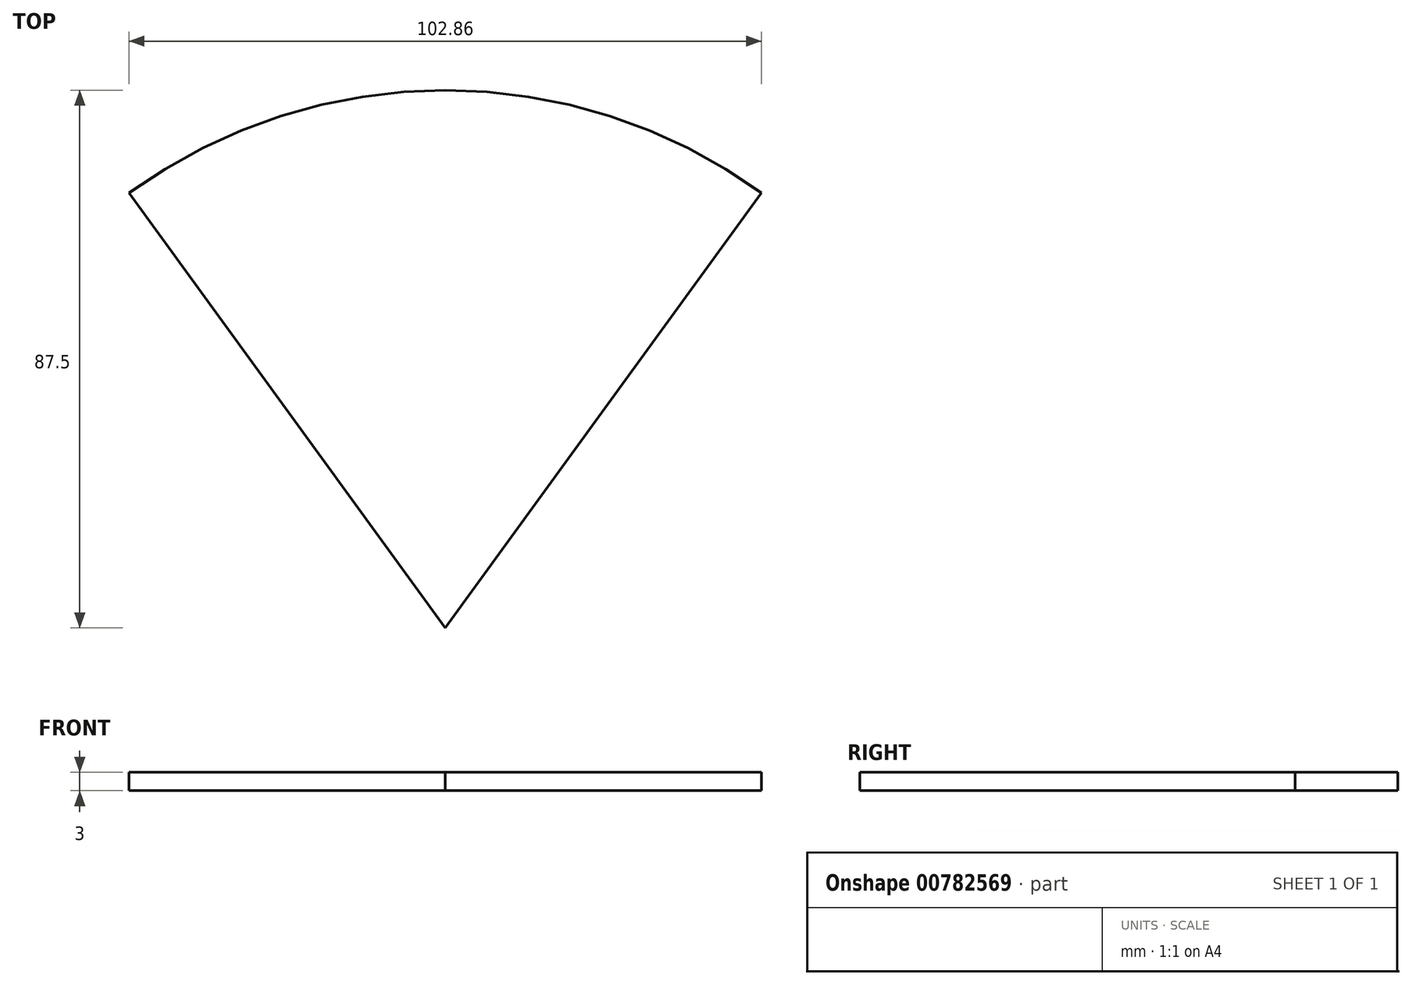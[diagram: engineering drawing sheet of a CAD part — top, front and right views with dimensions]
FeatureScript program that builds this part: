
annotation { "Feature Type Name" : "Feature", "Feature Type Description" : "" }
export const myFeature = defineFeature(function(context is Context, id is Id, definition is map)
    precondition{}
    {
        {
            var Q0;
            Q0=qCreatedBy(makeId("Top.planeOp"),FACE);
            var sketch = newSketch(context, id + "F0", { "sketchPlane" : qUnion([Q0])});
            skArc(sketch, "E0", {"start": v(51.43, 70.79) * mm, "mid": v(0, 87.5) * mm, "end": v(-51.43, 70.79) * mm});
            skLineSegment(sketch, "E1", {"start": v(0, 0) * mm, "end": v(-120.56, 0) * mm});
            skLineSegment(sketch, "E2", {"start": v(-120.56, 0) * mm, "end": v(117.7, 0) * mm, "construction": true});
            skLineSegment(sketch, "E3", {"start": v(0, -87.5) * mm, "end": v(0, 102.9) * mm});
            skLineSegment(sketch, "E4", {"start": v(0, 102.9) * mm, "end": v(0, -98.98) * mm, "construction": true});
            skLineSegment(sketch, "E5", {"start": v(0, 0) * mm, "end": v(51.43, 70.79) * mm});
            skLineSegment(sketch, "E6.MirrorCS", {"start": v(0, 0) * mm, "end": v(-51.43, 70.79) * mm});
            skSolve(sketch);
        }
        {
            var Q0;
            Q0 = qSketchRegion(id + "F0", true);
            extrude(context, id + "F1", {"entities" : qUnion([Q0]), "depth" : 3 * mm, "offsetDistance" : 25 * mm});
        }
    });
